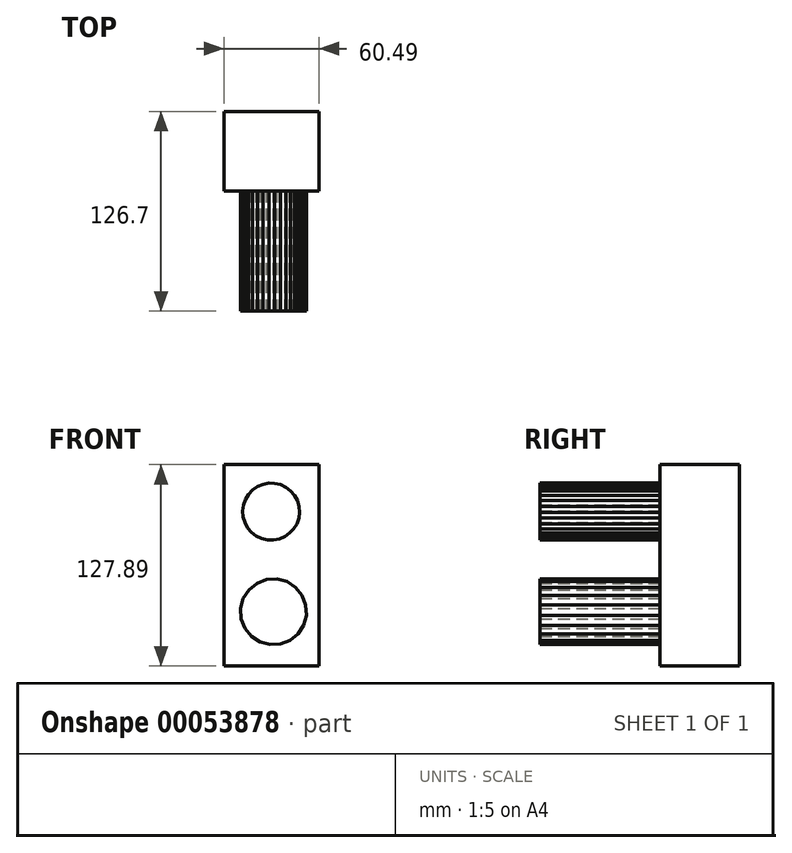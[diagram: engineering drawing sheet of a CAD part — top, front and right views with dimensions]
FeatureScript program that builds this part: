
annotation { "Feature Type Name" : "Feature", "Feature Type Description" : "" }
export const myFeature = defineFeature(function(context is Context, id is Id, definition is map)
    precondition{}
    {
        {
            var Q0;
            Q0=qCreatedBy(makeId("Top.planeOp"),FACE);
            var sketch = newSketch(context, id + "F0", { "sketchPlane" : qUnion([Q0])});
            skLineSegment(sketch, "E0", {"start": v(0, 0) * mm, "end": v(0, 50.5) * mm});
            skLineSegment(sketch, "E1", {"start": v(0, 50.5) * mm, "end": v(60.5, 50.5) * mm});
            skLineSegment(sketch, "E2", {"start": v(60.5, 50.5) * mm, "end": v(60.5, 0) * mm});
            skLineSegment(sketch, "E3", {"start": v(60.5, 0) * mm, "end": v(0, 0) * mm});
            skSolve(sketch);
        }
        {
            var Q0;
            Q0=makeQuery(id+"F0.imprint","IMPRINT",FACE,{"disambiguationData":[TD([[makeQuery(id+"F0.imprint","IMPRINT",EDGE,{"derivedFrom":sQuery(id+"F0.wireOp",EDGE,"E0")}),-1.0]])]});
            extrude(context, id + "F1", {"entities" : qUnion([Q0]), "depth" : 127.89 * mm});
        }
        {
            var Q0;
            Q0=makeQuery(id+"F1.opExtrude","SWEPT_FACE",FACE,{"disambiguationData":[OSD([sQuery(id+"F0.wireOp",EDGE,"E3")])]});
            var sketch = newSketch(context, id + "F2", { "sketchPlane" : qUnion([Q0])});
            skCircle(sketch, "E4.cCircle", {"center": v(29.98, 98.06) * mm, "radius": 17.99 * mm, "construction": true});
            skLineSegment(sketch, "E4.0", {"start": v(38.66, 82.19) * mm, "end": v(35.17, 80.73) * mm});
            skLineSegment(sketch, "E4.1", {"start": v(35.17, 80.73) * mm, "end": v(31.45, 80.03) * mm});
            skLineSegment(sketch, "E4.2", {"start": v(31.45, 80.03) * mm, "end": v(27.67, 80.12) * mm});
            skLineSegment(sketch, "E4.3", {"start": v(27.67, 80.12) * mm, "end": v(24, 80.99) * mm});
            skLineSegment(sketch, "E4.4", {"start": v(24, 80.99) * mm, "end": v(20.57, 82.6) * mm});
            skLineSegment(sketch, "E4.5", {"start": v(20.57, 82.6) * mm, "end": v(17.57, 84.9) * mm});
            skLineSegment(sketch, "E4.6", {"start": v(17.57, 84.9) * mm, "end": v(15.1, 87.77) * mm});
            skLineSegment(sketch, "E4.7", {"start": v(15.1, 87.77) * mm, "end": v(13.29, 91.08) * mm});
            skLineSegment(sketch, "E4.8", {"start": v(13.29, 91.08) * mm, "end": v(12.2, 94.7) * mm});
            skLineSegment(sketch, "E4.9", {"start": v(12.2, 94.7) * mm, "end": v(11.9, 98.47) * mm});
            skLineSegment(sketch, "E4.10", {"start": v(11.9, 98.47) * mm, "end": v(12.37, 102.23) * mm});
            skLineSegment(sketch, "E4.11", {"start": v(12.37, 102.23) * mm, "end": v(13.63, 105.8) * mm});
            skLineSegment(sketch, "E4.12", {"start": v(13.63, 105.8) * mm, "end": v(15.6, 109.02) * mm});
            skLineSegment(sketch, "E4.13", {"start": v(15.6, 109.02) * mm, "end": v(18.19, 111.78) * mm});
            skLineSegment(sketch, "E4.14", {"start": v(18.19, 111.78) * mm, "end": v(21.3, 113.93) * mm});
            skLineSegment(sketch, "E4.15", {"start": v(21.3, 113.93) * mm, "end": v(24.78, 115.39) * mm});
            skLineSegment(sketch, "E4.16", {"start": v(24.78, 115.39) * mm, "end": v(28.5, 116.09) * mm});
            skLineSegment(sketch, "E4.17", {"start": v(28.5, 116.09) * mm, "end": v(32.28, 116) * mm});
            skLineSegment(sketch, "E4.18", {"start": v(32.28, 116) * mm, "end": v(35.96, 115.13) * mm});
            skLineSegment(sketch, "E4.19", {"start": v(35.96, 115.13) * mm, "end": v(39.38, 113.51) * mm});
            skLineSegment(sketch, "E4.20", {"start": v(39.38, 113.51) * mm, "end": v(42.39, 111.22) * mm});
            skLineSegment(sketch, "E4.21", {"start": v(42.39, 111.22) * mm, "end": v(44.85, 108.35) * mm});
            skLineSegment(sketch, "E4.22", {"start": v(44.85, 108.35) * mm, "end": v(46.67, 105.03) * mm});
            skLineSegment(sketch, "E4.23", {"start": v(46.67, 105.03) * mm, "end": v(47.75, 101.41) * mm});
            skLineSegment(sketch, "E4.24", {"start": v(47.75, 101.41) * mm, "end": v(48.06, 97.64) * mm});
            skLineSegment(sketch, "E4.25", {"start": v(48.06, 97.64) * mm, "end": v(47.58, 93.9) * mm});
            skLineSegment(sketch, "E4.26", {"start": v(47.58, 93.9) * mm, "end": v(46.33, 90.32) * mm});
            skLineSegment(sketch, "E4.27", {"start": v(46.33, 90.32) * mm, "end": v(44.36, 87.1) * mm});
            skLineSegment(sketch, "E4.28", {"start": v(44.36, 87.1) * mm, "end": v(41.77, 84.34) * mm});
            skLineSegment(sketch, "E4.29", {"start": v(41.77, 84.34) * mm, "end": v(38.66, 82.19) * mm});
            skPoint(sketch, "E4.0.midPoint", {"position": v(36.91, 81.46) * mm});
            skCircle(sketch, "E5.cCircle", {"center": v(31.46, 34.4) * mm, "radius": 20.7 * mm, "construction": true});
            skLineSegment(sketch, "E5.0", {"start": v(41.95, 16.24) * mm, "end": v(35.83, 13.89) * mm});
            skLineSegment(sketch, "E5.1", {"start": v(35.83, 13.89) * mm, "end": v(29.28, 13.54) * mm});
            skLineSegment(sketch, "E5.2", {"start": v(29.28, 13.54) * mm, "end": v(22.95, 15.24) * mm});
            skLineSegment(sketch, "E5.3", {"start": v(22.95, 15.24) * mm, "end": v(17.45, 18.8) * mm});
            skLineSegment(sketch, "E5.4", {"start": v(17.45, 18.8) * mm, "end": v(13.32, 23.9) * mm});
            skLineSegment(sketch, "E5.5", {"start": v(13.32, 23.9) * mm, "end": v(10.96, 30.02) * mm});
            skLineSegment(sketch, "E5.6", {"start": v(10.96, 30.02) * mm, "end": v(10.61, 36.57) * mm});
            skLineSegment(sketch, "E5.7", {"start": v(10.61, 36.57) * mm, "end": v(12.3, 42.9) * mm});
            skLineSegment(sketch, "E5.8", {"start": v(12.3, 42.9) * mm, "end": v(15.88, 48.4) * mm});
            skLineSegment(sketch, "E5.9", {"start": v(15.88, 48.4) * mm, "end": v(20.97, 52.54) * mm});
            skLineSegment(sketch, "E5.10", {"start": v(20.97, 52.54) * mm, "end": v(27.1, 54.9) * mm});
            skLineSegment(sketch, "E5.11", {"start": v(27.1, 54.9) * mm, "end": v(33.64, 55.24) * mm});
            skLineSegment(sketch, "E5.12", {"start": v(33.64, 55.24) * mm, "end": v(39.98, 53.55) * mm});
            skLineSegment(sketch, "E5.13", {"start": v(39.98, 53.55) * mm, "end": v(45.48, 49.98) * mm});
            skLineSegment(sketch, "E5.14", {"start": v(45.48, 49.98) * mm, "end": v(49.6, 44.88) * mm});
            skLineSegment(sketch, "E5.15", {"start": v(49.6, 44.88) * mm, "end": v(51.96, 38.76) * mm});
            skLineSegment(sketch, "E5.16", {"start": v(51.96, 38.76) * mm, "end": v(52.31, 32.21) * mm});
            skLineSegment(sketch, "E5.17", {"start": v(52.31, 32.21) * mm, "end": v(50.62, 25.88) * mm});
            skLineSegment(sketch, "E5.18", {"start": v(50.62, 25.88) * mm, "end": v(47.05, 20.37) * mm});
            skLineSegment(sketch, "E5.19", {"start": v(47.05, 20.37) * mm, "end": v(41.95, 16.24) * mm});
            skPoint(sketch, "E5.0.midPoint", {"position": v(38.9, 15.07) * mm});
            skSolve(sketch);
        }
        {
            var Q0;
            Q0 = qSketchRegion(id + "F2", true);
            extrude(context, id + "F3", {"entities" : qUnion([Q0]), "operationType" : NewBodyOperationType.ADD, "depth" : 76.2 * mm});
        }
    });
